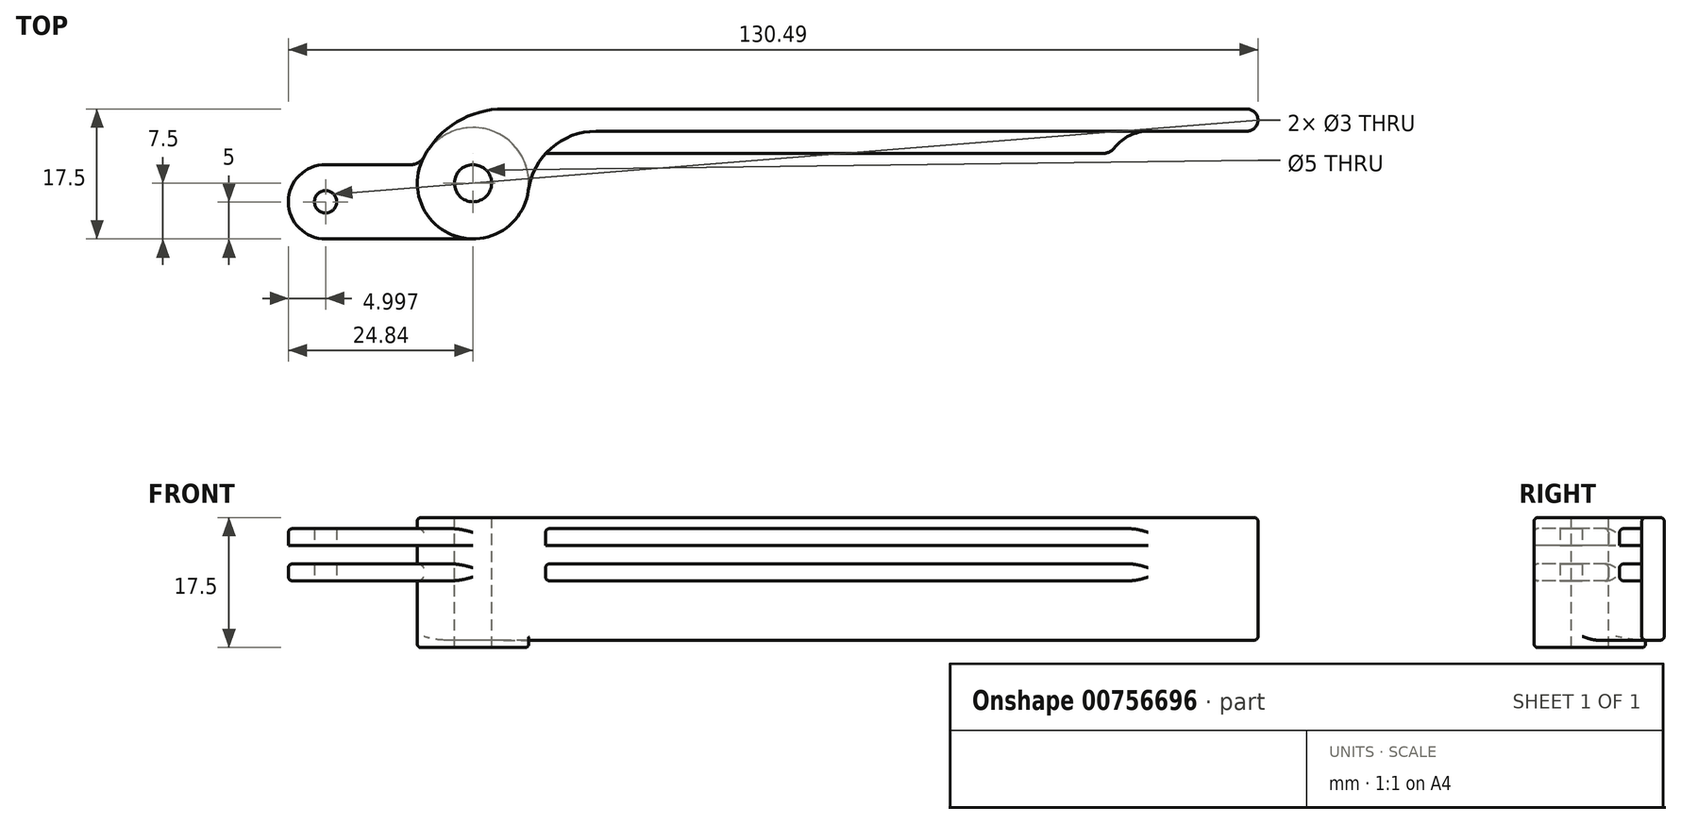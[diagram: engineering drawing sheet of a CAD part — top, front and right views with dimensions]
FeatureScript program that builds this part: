
annotation { "Feature Type Name" : "Feature", "Feature Type Description" : "" }
export const myFeature = defineFeature(function(context is Context, id is Id, definition is map)
    precondition{}
    {
        {
            var Q0;
            Q0=qCreatedBy(makeId("Top.planeOp"),FACE);
            var sketch = newSketch(context, id + "F0", { "sketchPlane" : qUnion([Q0])});
            skCircle(sketch, "E0", {"center": v(0, 0) * mm, "radius": 20 * mm, "construction": true});
            skLineSegment(sketch, "E1", {"start": v(0, -7.5) * mm, "end": v(133.22, -7.5) * mm});
            skArc(sketch, "E2", {"start": v(0, -7.5) * mm, "mid": v(4.94, -5.65) * mm, "end": v(7.43, -1) * mm});
            skArc(sketch, "E3", {"start": v(16.58, 7) * mm, "mid": v(10.5, 4.72) * mm, "end": v(7.43, -1) * mm});
            skLineSegment(sketch, "E4", {"start": v(16.58, 7) * mm, "end": v(104.15, 7) * mm});
            skLineSegment(sketch, "E5", {"start": v(4.15, 10) * mm, "end": v(104.15, 10) * mm});
            skArc(sketch, "E6", {"start": v(104.15, 7) * mm, "mid": v(105.65, 8.5) * mm, "end": v(104.15, 10) * mm});
            skLineSegment(sketch, "E7", {"start": v(-28.1, 7.5) * mm, "end": v(105.43, 7.5) * mm, "construction": true});
            skCircle(sketch, "E8.0", {"center": v(0, 0) * mm, "radius": 2.5 * mm});
            skCircle(sketch, "E9", {"center": v(0, 0) * mm, "radius": 7.5 * mm, "construction": true});
            skArc(sketch, "E10", {"start": v(4.15, 10) * mm, "mid": v(-2.15, 8.25) * mm, "end": v(-6.63, 3.5) * mm});
            skArc(sketch, "E11", {"start": v(-8.3, 2.5) * mm, "mid": v(-7.32, 2.77) * mm, "end": v(-6.63, 3.5) * mm, "construction": true});
            skLineSegment(sketch, "E12", {"start": v(-8.3, 2.5) * mm, "end": v(-19.84, 2.5) * mm, "construction": true});
            skLineSegment(sketch, "E13", {"start": v(0, -7.5) * mm, "end": v(-19.84, -7.5) * mm, "construction": true});
            skArc(sketch, "E14", {"start": v(-19.84, 2.5) * mm, "mid": v(-24.84, -2.5) * mm, "end": v(-19.84, -7.5) * mm, "construction": true});
            skCircle(sketch, "E15", {"center": v(-19.84, -2.5) * mm, "radius": 1.5 * mm, "construction": true});
            skArc(sketch, "E16", {"start": v(-6.63, 3.5) * mm, "mid": v(-6.42, -3.87) * mm, "end": v(0, -7.5) * mm});
            skSolve(sketch);
        }
        {
            var Q0;
            Q0 = qSketchRegion(id + "F0", true);
            extrude(context, id + "F1", {"entities" : qUnion([Q0]), "oppositeDirection" : true, "depth" : 11.5 * mm, "offsetDistance" : 25 * mm, "hasSecondDirection" : true, "secondDirectionOppositeDirection" : false, "secondDirectionDepth" : 5 * mm});
        }
        {
            var Q0;
            Q0=qCreatedBy(makeId("Top.planeOp"),FACE);
            var sketch = newSketch(context, id + "F2", { "sketchPlane" : qUnion([Q0])});
            skCircle(sketch, "E17.0", {"center": v(0, 0) * mm, "radius": 2.5 * mm});
            skCircle(sketch, "E18", {"center": v(0, 0) * mm, "radius": 7.5 * mm});
            skSolve(sketch);
        }
        {
            var Q0;
            Q0 = qSketchRegion(id + "F2", true);
            extrude(context, id + "F3", {"entities" : qUnion([Q0]), "operationType" : NewBodyOperationType.ADD, "oppositeDirection" : true, "depth" : 12.5 * mm, "offsetDistance" : 25 * mm});
        }
        {
            var Q0;
            Q0=qCreatedBy(makeId("Top.planeOp"),FACE);
            var sketch = newSketch(context, id + "F4", { "sketchPlane" : qUnion([Q0])});
            skArc(sketch, "E19.0", {"start": v(-8.3, 2.5) * mm, "mid": v(-7.32, 2.77) * mm, "end": v(-6.63, 3.5) * mm});
            skLineSegment(sketch, "E19.1", {"start": v(-8.3, 2.5) * mm, "end": v(-19.84, 2.5) * mm});
            skArc(sketch, "E19.2", {"start": v(-19.84, 2.5) * mm, "mid": v(-24.84, -2.5) * mm, "end": v(-19.84, -7.5) * mm});
            skLineSegment(sketch, "E19.3", {"start": v(0, -7.5) * mm, "end": v(-19.84, -7.5) * mm});
            skArc(sketch, "E20", {"start": v(-6.63, 3.5) * mm, "mid": v(-6.42, -3.87) * mm, "end": v(0, -7.5) * mm});
            skCircle(sketch, "E21.0", {"center": v(-19.84, -2.5) * mm, "radius": 1.5 * mm});
            skLineSegment(sketch, "E22", {"start": v(84.7, 4) * mm, "end": v(9.77, 4) * mm});
            skArc(sketch, "E23", {"start": v(16.58, 7) * mm, "mid": v(12.86, 6.22) * mm, "end": v(9.77, 4) * mm});
            skLineSegment(sketch, "E24", {"start": v(16.58, 7) * mm, "end": v(90.88, 7) * mm});
            skArc(sketch, "E25", {"start": v(84.7, 4) * mm, "mid": v(85.63, 4.21) * mm, "end": v(86.38, 4.81) * mm});
            skArc(sketch, "E26", {"start": v(90.88, 7) * mm, "mid": v(88.38, 6.42) * mm, "end": v(86.38, 4.81) * mm});
            skSolve(sketch);
        }
        {
            var Q0;
            Q0 = qSketchRegion(id + "F4", true);
            extrude(context, id + "F5", {"entities" : qUnion([Q0]), "operationType" : NewBodyOperationType.ADD, "depth" : 3.5 * mm, "offsetDistance" : 25 * mm, "hasSecondDirection" : true, "secondDirectionOppositeDirection" : true, "secondDirectionDepth" : 3.5 * mm});
        }
        {
            var Q0;
            Q0 = qSketchRegion(id + "F4", true);
            extrude(context, id + "F6", {"entities" : qUnion([Q0]), "operationType" : NewBodyOperationType.REMOVE, "oppositeDirection" : true, "depth" : 1.25 * mm, "offsetDistance" : 25 * mm, "hasSecondDirection" : true, "secondDirectionOppositeDirection" : false, "secondDirectionDepth" : 1.25 * mm});
        }
        {
            var Q0;
            Q0=makeQuery(id+"F1.opExtrude","CAP_EDGE",EDGE,{"disambiguationData":[OSD([sQuery(id+"F0.wireOp",EDGE,"E4")])],"isStart":false});
            var Q1;
            Q1=makeQuery(id+"F1.opExtrude","CAP_EDGE",EDGE,{"disambiguationData":[OSD([sQuery(id+"F0.wireOp",EDGE,"E5")])],"isStart":true});
            var Q2;
            Q2=makeQuery(id+"F5.opExtrude","CAP_EDGE",EDGE,{"disambiguationData":[OSD([sQuery(id+"F4.wireOp",EDGE,"E19.1")])],"isStart":false});
            var Q3;
            Q3=makeQuery(id+"F6.boolean.opBoolean","COPY",EDGE,{"derivedFrom":makeQuery(id+"F6.opExtrude","CAP_EDGE",EDGE,{"disambiguationData":[OSD([sQuery(id+"F4.wireOp",EDGE,"E19.2")])],"isStart":true})});
            var Q4;
            Q4=makeQuery(id+"F6.boolean.opBoolean","COPY",EDGE,{"derivedFrom":makeQuery(id+"F6.opExtrude","CAP_EDGE",EDGE,{"disambiguationData":[OSD([sQuery(id+"F4.wireOp",EDGE,"E19.2")])],"isStart":false})});
            var Q5;
            Q5=makeQuery(id+"F5.opExtrude","CAP_EDGE",EDGE,{"disambiguationData":[OSD([sQuery(id+"F4.wireOp",EDGE,"E19.2")])],"isStart":true});
            var Q6;
            Q6=makeQuery(id+"F3.opExtrude","CAP_EDGE",EDGE,{"disambiguationData":[OSD([sQuery(id+"F2.wireOp",EDGE,"E18")])],"isStart":false});
            var Q7;
            Q7=makeQuery(id+"F3.opExtrude","CAP_EDGE",EDGE,{"disambiguationData":[OSD([sQuery(id+"F2.wireOp",EDGE,"E18")])],"isStart":true});
            var Q8;
            Q8=makeQuery(id+"F5.opExtrude","CAP_EDGE",EDGE,{"disambiguationData":[OSD([sQuery(id+"F4.wireOp",EDGE,"E22")])],"isStart":false});
            var Q9;
            Q9=makeQuery(id+"F6.boolean.opBoolean","COPY",EDGE,{"derivedFrom":makeQuery(id+"F6.opExtrude","CAP_EDGE",EDGE,{"disambiguationData":[OSD([sQuery(id+"F4.wireOp",EDGE,"E22")])],"isStart":true})});
            var Q10;
            Q10=makeQuery(id+"F6.boolean.opBoolean","COPY",EDGE,{"derivedFrom":makeQuery(id+"F6.opExtrude","CAP_EDGE",EDGE,{"disambiguationData":[OSD([sQuery(id+"F4.wireOp",EDGE,"E22")])],"isStart":false})});
            var Q11;
            Q11=makeQuery(id+"F5.opExtrude","CAP_EDGE",EDGE,{"disambiguationData":[OSD([sQuery(id+"F4.wireOp",EDGE,"E22")])],"isStart":true});
            fillet(context, id + "F7", {"entities" : qUnion([Q0, Q1, Q2, Q3, Q4, Q5, Q6, Q7, Q8, Q9, Q10, Q11]), "radius" : 0.5 * mm, "tangentPropagation" : true, "allowEdgeOverflow" : false});
        }
    });
